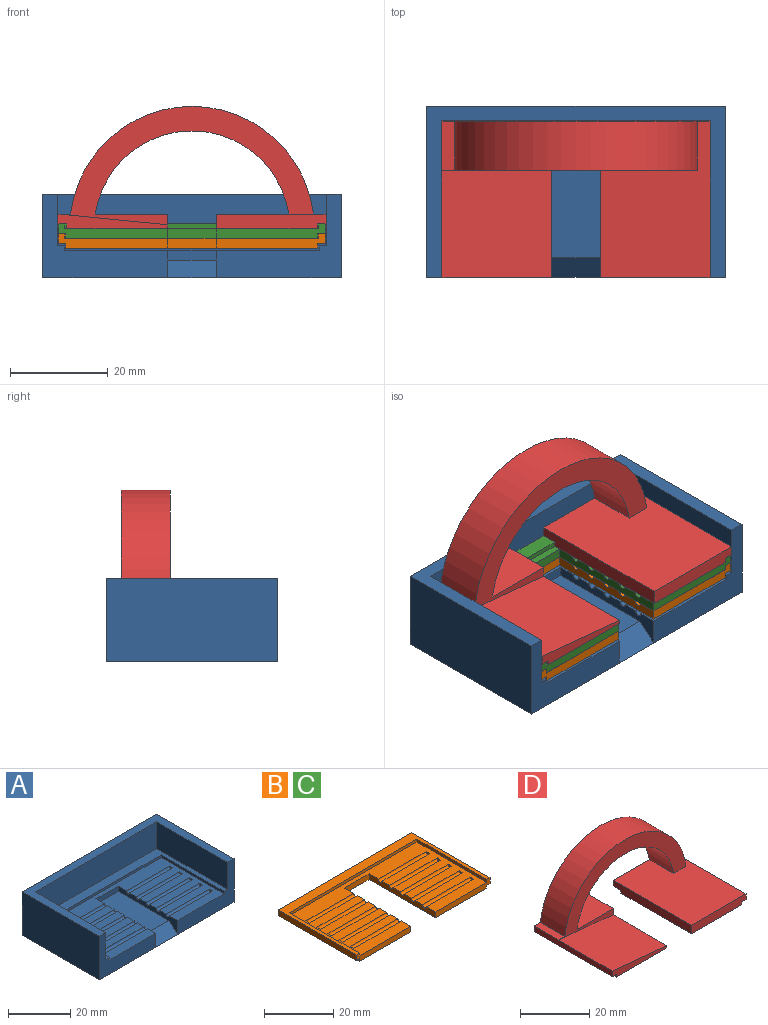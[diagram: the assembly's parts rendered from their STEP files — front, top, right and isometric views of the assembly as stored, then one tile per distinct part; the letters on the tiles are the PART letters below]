
ASSEMBLY  parts=4 mates=3
PART A: 40 faces, bbox 61x35x17 mm
  f0: plane 25.5x17mm, normal (0,-1,0), area 176.3mm2, adj f1,f4,f5,f8,f10,f11,f12,f19
  f1: plane 52x28.5mm, normal (0,0,1), area 919.5mm2, adj f0,f2,f3,f11,f14,f17,f18,f19
  f2: plane 28.5x1mm, normal (1,0,0), area 28.5mm2, adj f1,f3,f10,f14
  f3: plane 25.5x17mm, normal (0,-1,0), area 176.2mm2, adj f1,f2,f4,f7,f8,f9,f10,f18
  f4: plane 61x35mm, normal (0,0,1), area 375mm2, adj f0,f3,f5,f6,f7,f9,f12,f13
  f5: plane 35x17mm, normal (1,0,0), area 595mm2, adj f0,f4,f6,f8
  f6: plane 61x17mm, normal (0,1,0), area 1037mm2, adj f4,f5,f7,f8
  f7: plane 35x17mm, normal (-1,0,0), area 595mm2, adj f3,f4,f6,f8
  f8: plane 61x35mm, normal (0,0,-1), area 2135mm2, adj f0,f3,f5,f6,f7,f15
  f9: plane 32x10.5mm, normal (1,0,0), area 336mm2, adj f3,f4,f10,f13
  f10: plane 55x32mm, normal (0,0,1), area 278mm2, adj f0,f2,f3,f9,f11,f12,f13,f14
  f11: plane 28.5x1mm, normal (-1,0,0), area 28.5mm2, adj f0,f1,f10,f14
  f12: plane 32x10.5mm, normal (-1,0,0), area 336mm2, adj f0,f4,f10,f13
  f13: plane 55x10.5mm, normal (0,-1,0), area 577.5mm2, adj f4,f9,f10,f12
  f14: plane 52x1mm, normal (0,-1,0), area 52mm2, adj f1,f2,f10,f11
  f15: plane 10x4mm, normal (0,-0.66,0.75), area 53.2mm2, adj f8,f16,f18,f19
  f16: plane 23x10mm, normal (0,0,1), area 230mm2, adj f15,f17,f18,f19
  f17: plane 10x2mm, normal (0,-1,0), area 20mm2, adj f1,f16,f18,f19
  f18: plane 27x5.5mm, normal (1,0,0), area 56.6mm2, adj f1,f3,f15,f16,f17,f31,f33,f35
  f19: plane 27x5.5mm, normal (-1,0,0), area 56.6mm2, adj f0,f1,f15,f16,f17,f20,f22,f24
  f20: cylinder r=0.75mm len=19.5mm, axis (1,0,0), area 45.9mm2, adj f1,f19,f21
  f21: plane 1.5x0.75mm, normal (-1,0,0), area 0.9mm2, adj f1,f20
  f22: cylinder r=0.75mm len=19.5mm, axis (1,0,0), area 45.9mm2, adj f1,f19,f23
  f23: plane 1.5x0.75mm, normal (-1,0,0), area 0.9mm2, adj f1,f22
  f24: cylinder r=0.75mm len=19.5mm, axis (1,0,0), area 45.9mm2, adj f1,f19,f25
  f25: plane 1.5x0.75mm, normal (-1,0,0), area 0.9mm2, adj f1,f24
  f26: cylinder r=0.75mm len=19.5mm, axis (1,0,0), area 45.9mm2, adj f1,f19,f27
  f27: plane 1.5x0.75mm, normal (-1,0,0), area 0.9mm2, adj f1,f26
  f28: cylinder r=0.75mm len=19.5mm, axis (1,0,0), area 45.9mm2, adj f1,f19,f29
  f29: plane 1.5x0.75mm, normal (-1,0,0), area 0.9mm2, adj f1,f28
  f30: plane 1.5x0.75mm, normal (1,0,0), area 0.9mm2, adj f1,f31
  f31: cylinder r=0.75mm len=19.5mm, axis (1,0,0), area 45.9mm2, adj f1,f18,f30
  f32: plane 1.5x0.75mm, normal (1,0,0), area 0.9mm2, adj f1,f33
  f33: cylinder r=0.75mm len=19.5mm, axis (1,0,0), area 45.9mm2, adj f1,f18,f32
  f34: plane 1.5x0.75mm, normal (1,0,0), area 0.9mm2, adj f1,f35
  f35: cylinder r=0.75mm len=19.5mm, axis (1,0,0), area 45.9mm2, adj f1,f18,f34
  f36: plane 1.5x0.75mm, normal (1,0,0), area 0.9mm2, adj f1,f37
  f37: cylinder r=0.75mm len=19.5mm, axis (1,0,0), area 45.9mm2, adj f1,f18,f36
  f38: plane 1.5x0.75mm, normal (1,0,0), area 0.9mm2, adj f1,f39
  f39: cylinder r=0.75mm len=19.5mm, axis (1,0,0), area 45.9mm2, adj f1,f18,f38
PART B: 38 faces, bbox 54.6x31.8x3 mm
  f0: plane 22.3x3mm, normal (0,-1,0), area 44.4mm2, adj f2,f3,f4,f5,f7,f10,f14,f15
  f1: plane 22.3x3mm, normal (0,-1,0), area 44.4mm2, adj f2,f3,f4,f5,f6,f9,f12,f16
  f2: plane 52x28.5mm, normal (0,0,1), area 919.5mm2, adj f0,f1,f9,f10,f11,f15,f16,f17
  f3: plane 51.6x28.5mm, normal (0,0,-1), area 1200.6mm2, adj f0,f1,f12,f13,f14,f15,f16,f17
  f4: plane 54.6x31.8mm, normal (0,0,-1), area 265.7mm2, adj f0,f1,f6,f7,f8,f12,f13,f14
  f5: plane 54.6x31.8mm, normal (0,0,1), area 254.3mm2, adj f0,f1,f6,f7,f8,f9,f10,f11
  f6: plane 31.8x2mm, normal (-1,0,0), area 63.6mm2, adj f1,f4,f5,f8
  f7: plane 31.8x2mm, normal (1,0,0), area 63.6mm2, adj f0,f4,f5,f8
  f8: plane 54.6x2mm, normal (0,1,0), area 109.2mm2, adj f4,f5,f6,f7
  f9: plane 28.5x1mm, normal (1,0,0), area 28.5mm2, adj f1,f2,f5,f11
  f10: plane 28.5x1mm, normal (-1,0,0), area 28.5mm2, adj f0,f2,f5,f11
  f11: plane 52x1mm, normal (0,-1,0), area 52mm2, adj f2,f5,f9,f10
  f12: plane 28.5x1mm, normal (-1,0,0), area 28.5mm2, adj f1,f3,f4,f13
  f13: plane 51.6x1mm, normal (0,1,0), area 51.6mm2, adj f3,f4,f12,f14
  f14: plane 28.5x1mm, normal (1,0,0), area 28.5mm2, adj f0,f3,f4,f13
  f15: plane 27x2mm, normal (-1,0,0), area 49.6mm2, adj f0,f2,f3,f17,f28,f30,f32,f34
  f16: plane 27x2mm, normal (1,0,0), area 49.6mm2, adj f1,f2,f3,f17,f18,f20,f22,f24
  f17: plane 10x2mm, normal (0,-1,0), area 20mm2, adj f2,f3,f15,f16
  f18: cylinder r=0.75mm len=19.5mm, axis (1,0,0), area 45.9mm2, adj f2,f16,f19
  f19: plane 1.5x0.75mm, normal (1,0,0), area 0.9mm2, adj f2,f18
  f20: cylinder r=0.75mm len=19.5mm, axis (1,0,0), area 45.9mm2, adj f2,f16,f21
  f21: plane 1.5x0.75mm, normal (1,0,0), area 0.9mm2, adj f2,f20
  f22: cylinder r=0.75mm len=19.5mm, axis (1,0,0), area 45.9mm2, adj f2,f16,f23
  f23: plane 1.5x0.75mm, normal (1,0,0), area 0.9mm2, adj f2,f22
  f24: cylinder r=0.75mm len=19.5mm, axis (1,0,0), area 45.9mm2, adj f2,f16,f25
  f25: plane 1.5x0.75mm, normal (1,0,0), area 0.9mm2, adj f2,f24
  f26: cylinder r=0.75mm len=19.5mm, axis (1,0,0), area 45.9mm2, adj f2,f16,f27
  f27: plane 1.5x0.75mm, normal (1,0,0), area 0.9mm2, adj f2,f26
  f28: cylinder r=0.75mm len=19.5mm, axis (1,0,0), area 45.9mm2, adj f2,f15,f29
  f29: plane 1.5x0.75mm, normal (-1,0,0), area 0.9mm2, adj f2,f28
  f30: cylinder r=0.75mm len=19.5mm, axis (1,0,0), area 45.9mm2, adj f2,f15,f31
  f31: plane 1.5x0.75mm, normal (-1,0,0), area 0.9mm2, adj f2,f30
  f32: cylinder r=0.75mm len=19.5mm, axis (1,0,0), area 45.9mm2, adj f2,f15,f33
  f33: plane 1.5x0.75mm, normal (-1,0,0), area 0.9mm2, adj f2,f32
  f34: cylinder r=0.75mm len=19.5mm, axis (1,0,0), area 45.9mm2, adj f2,f15,f35
  f35: plane 1.5x0.75mm, normal (-1,0,0), area 0.9mm2, adj f2,f34
  f36: cylinder r=0.75mm len=19.5mm, axis (1,0,0), area 45.9mm2, adj f2,f15,f37
  f37: plane 1.5x0.75mm, normal (-1,0,0), area 0.9mm2, adj f2,f36
PART C: same geometry as B
PART D: 22 faces, bbox 54.8x32x25 mm
  f0: plane 32x3mm, normal (1,0,0), area 44.4mm2, adj f5,f6,f11,f12,f17,f18,f19,f20
  f1: plane 32x3mm, normal (-1,0,0), area 92.8mm2, adj f2,f7,f9,f10,f11,f21
  f2: plane 28.8x20.6mm, normal (0,0,-1), area 593.3mm2, adj f1,f3,f10,f21
  f3: plane 28.8x1mm, normal (1,0,0), area 28.8mm2, adj f2,f7,f10,f21
  f4: plane 28.8x1mm, normal (-1,0,0), area 28.8mm2, adj f5,f17,f18,f20
  f5: plane 28.8x20.6mm, normal (0,0,-1), area 593.3mm2, adj f0,f4,f18,f20
  f6: plane 14.77x10mm, normal (0,0,1), area 147.7mm2, adj f0,f11,f12,f13
  f7: plane 32x22.4mm, normal (0,0,-1), area 123.5mm2, adj f1,f3,f8,f10,f11,f21
  f8: plane 32x2mm, normal (1,0,0), area 64mm2, adj f7,f9,f10,f11
  f9: plane 32x22.4mm, normal (0,0,1), area 666.3mm2, adj f1,f8,f10,f11,f12,f13,f14
  f10: plane 22.4x3mm, normal (0,-1,0), area 65.4mm2, adj f1,f2,f3,f7,f8,f9
  f11: plane 54.8x24mm, normal (0,1,0), area 412.9mm2, adj f0,f1,f6,f7,f8,f9,f13,f14
  f12: plane 52.22x24.2mm, normal (0,-1,0), area 348mm2, adj f0,f6,f9,f13,f14,f15,f19
  f13: cylinder r=20mm len=39.55mm, axis (0,1,0), area 568.1mm2, adj f6,f9,f11,f12
  f14: cylinder r=25mm len=49.64mm, axis (0,1,0), area 725.3mm2, adj f9,f11,f12,f15
  f15: plane 10x2.58mm, normal (0,0,1), area 25.8mm2, adj f11,f12,f14,f16
  f16: plane 32x2mm, normal (-1,0,0), area 64mm2, adj f11,f15,f17,f18,f19
  f17: plane 32x22.4mm, normal (0,0,-1), area 123.5mm2, adj f0,f4,f11,f16,f18,f20
  f18: plane 22.4x3mm, normal (0,-1,0), area 40.8mm2, adj f0,f4,f5,f16,f17,f19
  f19: plane 22.4x22mm, normal (0.1,0,1), area 495.2mm2, adj f0,f12,f16,f18
  f20: plane 20.6x1mm, normal (0,1,0), area 20.6mm2, adj f0,f4,f5,f17
  f21: plane 20.6x1mm, normal (0,1,0), area 20.6mm2, adj f1,f2,f3,f7
PLACE A t=(-18.56,21.13,0)mm fixed
PLACE B t=(-18.61,21.23,7)mm
PLACE C t=(-18.61,21.23,9)mm
PLACE D t=(-18.56,53.03,10)mm
MATE slider A.f4 <-> C.f5  axis (0,0,1) through (-46.06,53.13,17)mm
MATE slider D.f15 <-> A.f4  axis (0,0,1) through (-45.96,53.03,13)mm
MATE slider A.f4 <-> B.f5  axis (0,0,1) through (-46.06,53.13,17)mm
